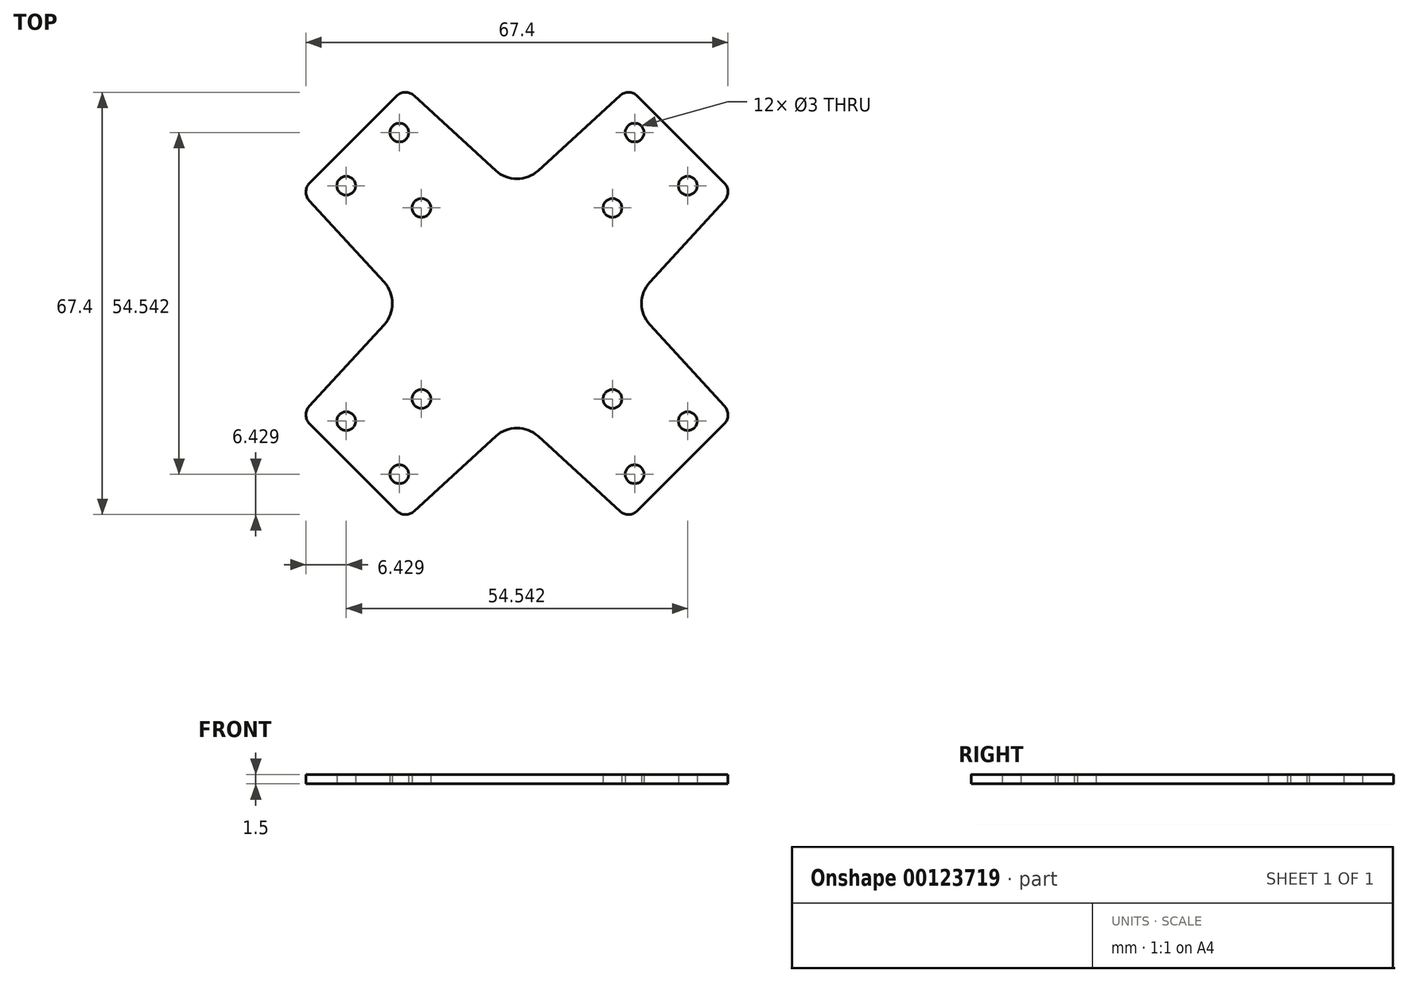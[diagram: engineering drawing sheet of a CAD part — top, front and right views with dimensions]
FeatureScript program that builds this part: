
annotation { "Feature Type Name" : "Feature", "Feature Type Description" : "" }
export const myFeature = defineFeature(function(context is Context, id is Id, definition is map)
    precondition{}
    {
        {
            var Q0;
            Q0=qCreatedBy(makeId("Top.planeOp"),FACE);
            var sketch = newSketch(context, id + "F0", { "sketchPlane" : qUnion([Q0])});
            skLineSegment(sketch, "E0", {"start": v(-42.43, -42.43) * mm, "end": v(42.43, 42.43) * mm, "construction": true});
            skLineSegment(sketch, "E1", {"start": v(-42.43, 42.43) * mm, "end": v(42.43, -42.43) * mm, "construction": true});
            skCircle(sketch, "E2", {"center": v(-15.25, 15.25) * mm, "radius": 1.5 * mm});
            skCircle(sketch, "E3.0.1.0", {"center": v(-15.25, -15.25) * mm, "radius": 1.5 * mm});
            skCircle(sketch, "E3.1.0.0", {"center": v(15.25, 15.25) * mm, "radius": 1.5 * mm});
            skCircle(sketch, "E3.1.1.0", {"center": v(15.25, -15.25) * mm, "radius": 1.5 * mm});
            skLineSegment(sketch, "E3.1.1.1", {"start": v(14.19, -14.19) * mm, "end": v(72.93, -72.93) * mm, "construction": true});
            skLineSegment(sketch, "E3.direction1", {"start": v(-15.25, 15.25) * mm, "end": v(15.25, 15.25) * mm, "construction": true});
            skLineSegment(sketch, "E3.direction2", {"start": v(-15.25, 15.25) * mm, "end": v(-15.25, -15.25) * mm, "construction": true});
            skLineSegment(sketch, "E4", {"start": v(-27.27, 18.79) * mm, "end": v(-18.79, 27.27) * mm, "construction": true});
            skLineSegment(sketch, "E5", {"start": v(18.79, 27.27) * mm, "end": v(27.27, 18.79) * mm, "construction": true});
            skLineSegment(sketch, "E6", {"start": v(18.79, -27.27) * mm, "end": v(27.27, -18.79) * mm, "construction": true});
            skLineSegment(sketch, "E7", {"start": v(-27.27, -18.79) * mm, "end": v(-18.79, -27.27) * mm, "construction": true});
            skCircle(sketch, "E8", {"center": v(-27.27, 18.79) * mm, "radius": 1.5 * mm});
            skCircle(sketch, "E9", {"center": v(-18.79, 27.27) * mm, "radius": 1.5 * mm});
            skCircle(sketch, "E10", {"center": v(18.79, 27.27) * mm, "radius": 1.5 * mm});
            skCircle(sketch, "E11", {"center": v(27.27, 18.79) * mm, "radius": 1.5 * mm});
            skCircle(sketch, "E12", {"center": v(27.27, -18.79) * mm, "radius": 1.5 * mm});
            skCircle(sketch, "E13", {"center": v(18.79, -27.27) * mm, "radius": 1.5 * mm});
            skCircle(sketch, "E14", {"center": v(-18.79, -27.27) * mm, "radius": 1.5 * mm});
            skCircle(sketch, "E15", {"center": v(-27.27, -18.79) * mm, "radius": 1.5 * mm});
            skPoint(sketch, "E16.endSnap0", {"position": v(-15.25, 0) * mm});
            skLineSegment(sketch, "E17", {"start": v(-34.47, -17.85) * mm, "end": v(-21.2, -3.38) * mm});
            skLineSegment(sketch, "E18", {"start": v(-17.85, -34.47) * mm, "end": v(-3.38, -21.2) * mm});
            skLineSegment(sketch, "E19.trimOffspring", {"start": v(3.38, -21.2) * mm, "end": v(17.85, -34.47) * mm});
            skLineSegment(sketch, "E20.trimOffspring", {"start": v(21.2, -3.38) * mm, "end": v(34.47, -17.85) * mm});
            skLineSegment(sketch, "E21.trimOffspring", {"start": v(3.38, 21.2) * mm, "end": v(17.85, 34.47) * mm});
            skPoint(sketch, "E22.orphan", {"position": v(-11.93, 11.93) * mm});
            skLineSegment(sketch, "E23", {"start": v(-17.85, 34.47) * mm, "end": v(-3.38, 21.2) * mm});
            skLineSegment(sketch, "E24", {"start": v(-34.47, 17.85) * mm, "end": v(-21.2, 3.38) * mm});
            skLineSegment(sketch, "E25", {"start": v(34.47, 17.85) * mm, "end": v(21.2, 3.38) * mm});
            skPoint(sketch, "E26.visualSharp", {"position": v(0, -18.11) * mm});
            skArc(sketch, "E26.filletArc", {"start": v(3.38, -21.2) * mm, "mid": v(0, -19.9) * mm, "end": v(-3.38, -21.2) * mm});
            skPoint(sketch, "E27.visualSharp", {"position": v(18.11, 0) * mm});
            skArc(sketch, "E27.filletArc", {"start": v(21.2, 3.38) * mm, "mid": v(19.9, 0) * mm, "end": v(21.2, -3.38) * mm});
            skPoint(sketch, "E28.visualSharp", {"position": v(-18.11, 0) * mm});
            skArc(sketch, "E28.filletArc", {"start": v(-21.2, -3.38) * mm, "mid": v(-19.9, 0) * mm, "end": v(-21.2, 3.38) * mm});
            skPoint(sketch, "E29.visualSharp", {"position": v(0, 18.11) * mm});
            skArc(sketch, "E29.filletArc", {"start": v(-3.38, 21.2) * mm, "mid": v(0, 19.9) * mm, "end": v(3.38, 21.2) * mm});
            skLineSegment(sketch, "E30", {"start": v(17.85, 34.47) * mm, "end": v(34.47, 17.85) * mm});
            skLineSegment(sketch, "E31", {"start": v(-34.47, 17.85) * mm, "end": v(-17.85, 34.47) * mm});
            skLineSegment(sketch, "E32", {"start": v(-34.47, -17.85) * mm, "end": v(-17.85, -34.47) * mm});
            skLineSegment(sketch, "E33", {"start": v(17.85, -34.47) * mm, "end": v(34.47, -17.85) * mm});
            skSolve(sketch);
        }
        {
            var Q0;
            Q0=qSketchRegion(id+"F0",true);
            extrude(context, id + "F1", {"entities" : qUnion([Q0]), "depth" : 1.5 * mm});
        }
        {
            var Q0;
            Q0=makeQuery(id+"F1.opExtrude","SWEPT_EDGE",EDGE,{"disambiguationData":[OSD([sQuery(id+"F0.wireOp",EDGE,"E24"),sQuery(id+"F0.wireOp",EDGE,"E31")])]});
            var Q1;
            Q1=makeQuery(id+"F1.opExtrude","SWEPT_EDGE",EDGE,{"disambiguationData":[OSD([sQuery(id+"F0.wireOp",EDGE,"E23"),sQuery(id+"F0.wireOp",EDGE,"E31")])]});
            var Q2;
            Q2=makeQuery(id+"F1.opExtrude","SWEPT_EDGE",EDGE,{"disambiguationData":[OSD([sQuery(id+"F0.wireOp",EDGE,"E21.trimOffspring"),sQuery(id+"F0.wireOp",EDGE,"E30")])]});
            var Q3;
            Q3=makeQuery(id+"F1.opExtrude","SWEPT_EDGE",EDGE,{"disambiguationData":[OSD([sQuery(id+"F0.wireOp",EDGE,"E25"),sQuery(id+"F0.wireOp",EDGE,"E30")])]});
            var Q4;
            Q4=makeQuery(id+"F1.opExtrude","SWEPT_EDGE",EDGE,{"disambiguationData":[OSD([sQuery(id+"F0.wireOp",EDGE,"E20.trimOffspring"),sQuery(id+"F0.wireOp",EDGE,"E33")])]});
            var Q5;
            Q5=makeQuery(id+"F1.opExtrude","SWEPT_EDGE",EDGE,{"disambiguationData":[OSD([sQuery(id+"F0.wireOp",EDGE,"E19.trimOffspring"),sQuery(id+"F0.wireOp",EDGE,"E33")])]});
            var Q6;
            Q6=makeQuery(id+"F1.opExtrude","SWEPT_EDGE",EDGE,{"disambiguationData":[OSD([sQuery(id+"F0.wireOp",EDGE,"E18"),sQuery(id+"F0.wireOp",EDGE,"E32")])]});
            var Q7;
            Q7=makeQuery(id+"F1.opExtrude","SWEPT_EDGE",EDGE,{"disambiguationData":[OSD([sQuery(id+"F0.wireOp",EDGE,"E17"),sQuery(id+"F0.wireOp",EDGE,"E32")])]});
            fillet(context, id + "F2", {"entities" : qUnion([Q0, Q1, Q2, Q3, Q4, Q5, Q6, Q7]), "radius" : 2 * mm, "tangentPropagation" : true, "allowEdgeOverflow" : false});
        }
    });
